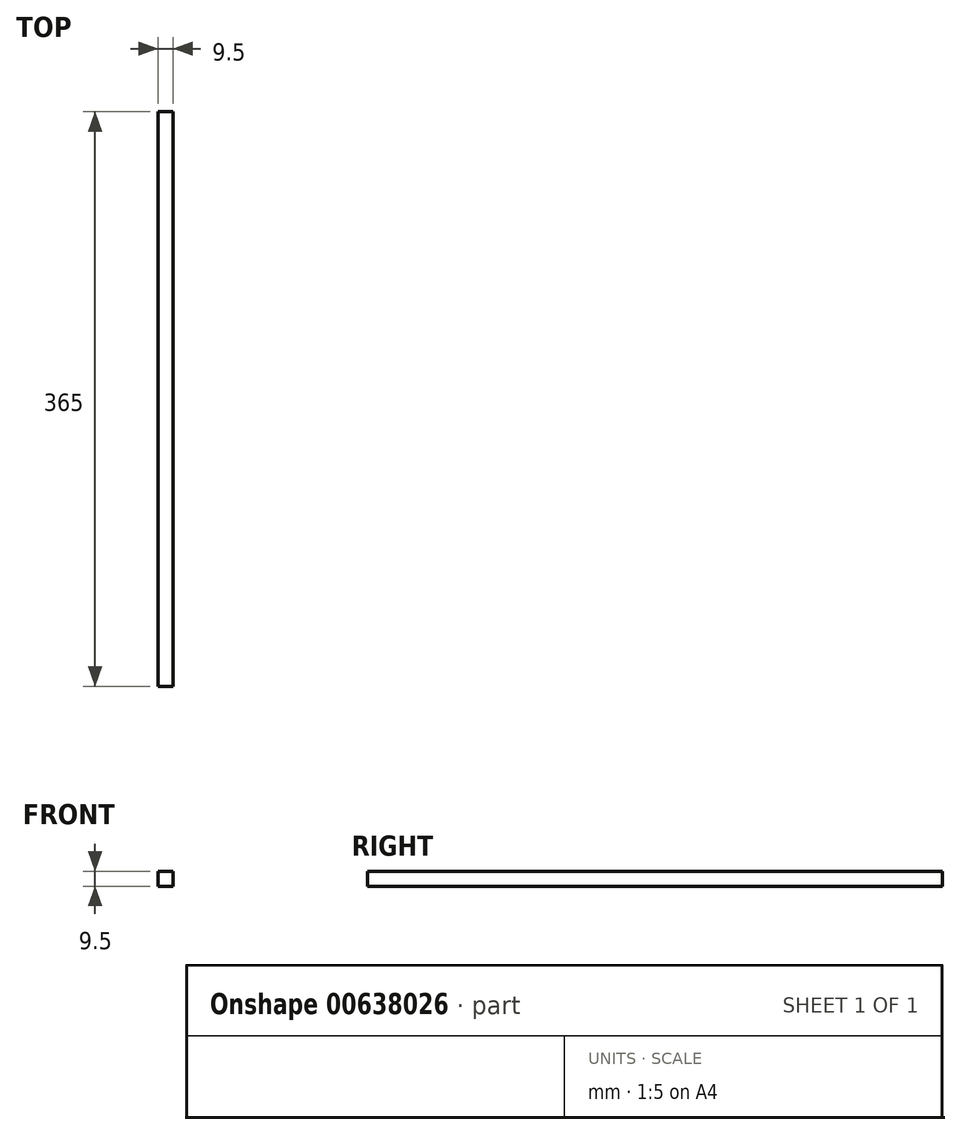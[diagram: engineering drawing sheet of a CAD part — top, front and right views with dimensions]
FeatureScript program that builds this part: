
annotation { "Feature Type Name" : "Feature", "Feature Type Description" : "" }
export const myFeature = defineFeature(function(context is Context, id is Id, definition is map)
    precondition{}
    {
        {
            var Q0;
            Q0=qCreatedBy(makeId("Front.planeOp"),FACE);
            var sketch = newSketch(context, id + "F0", { "sketchPlane" : qUnion([Q0])});
            skLineSegment(sketch, "E0.bottom", {"start": v(-45.16, 17.41) * mm, "end": v(-35.66, 17.41) * mm});
            skLineSegment(sketch, "E0.top", {"start": v(-45.16, 7.91) * mm, "end": v(-35.66, 7.91) * mm});
            skLineSegment(sketch, "E0.left", {"start": v(-45.16, 17.41) * mm, "end": v(-45.16, 7.91) * mm});
            skLineSegment(sketch, "E0.right", {"start": v(-35.66, 17.41) * mm, "end": v(-35.66, 7.91) * mm});
            skSolve(sketch);
        }
        {
            var Q0;
            Q0=makeQuery(id+"F0.imprint","IMPRINT",FACE,{"disambiguationData":[TD([[makeQuery(id+"F0.imprint","IMPRINT",EDGE,{"derivedFrom":sQuery(id+"F0.wireOp",EDGE,"E0.bottom")}),-1.0]])]});
            extrude(context, id + "F1", {"entities" : qUnion([Q0]), "depth" : 365 * mm, "offsetDistance" : 25 * mm});
        }
    });
